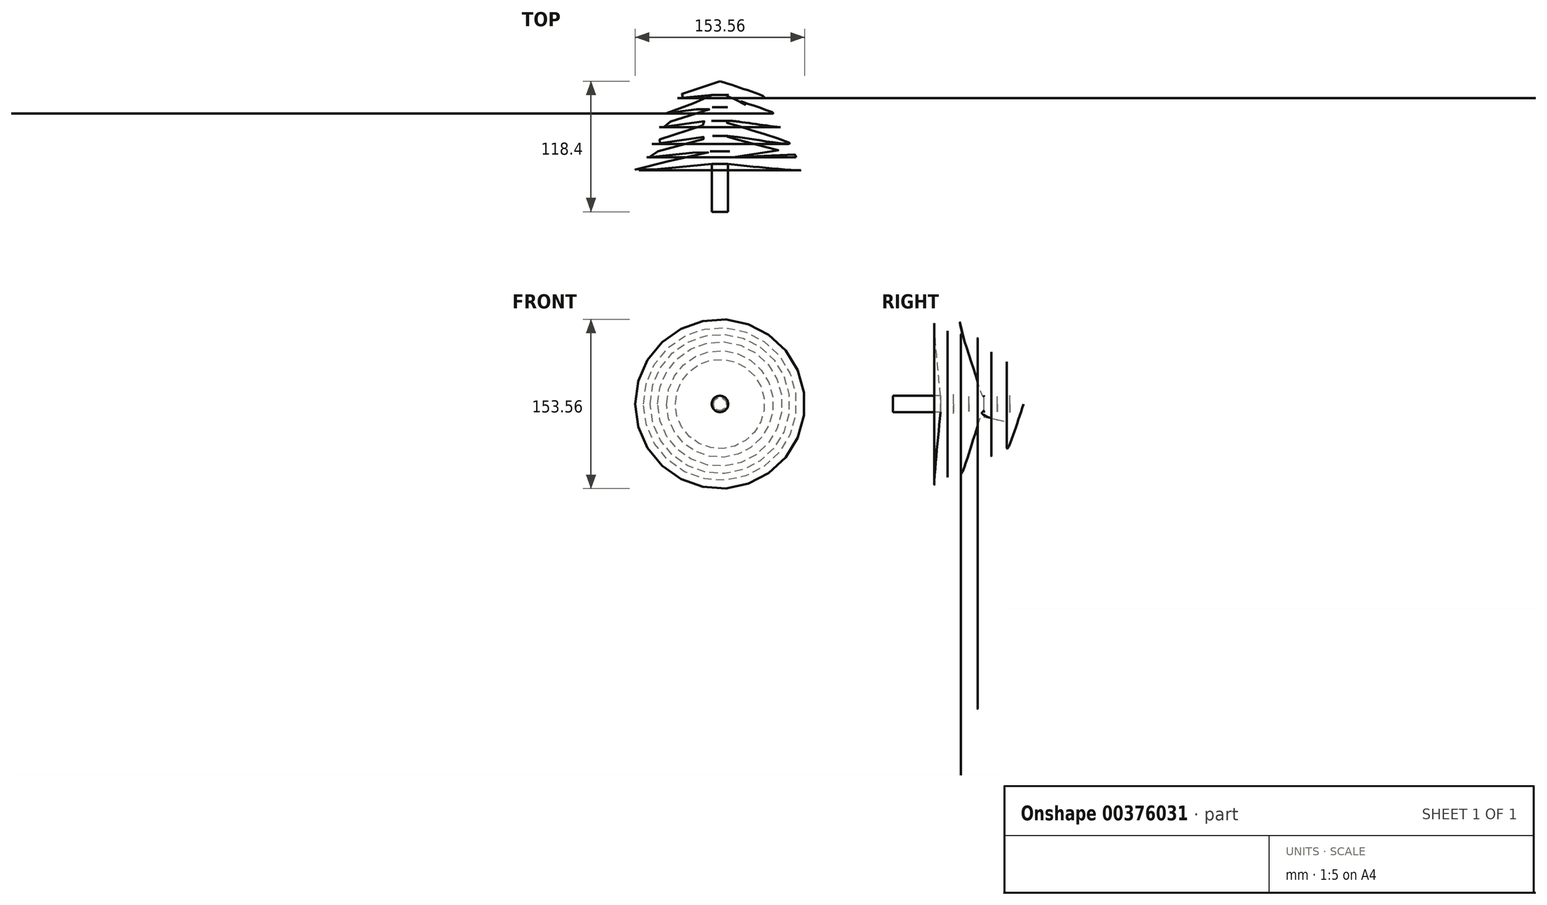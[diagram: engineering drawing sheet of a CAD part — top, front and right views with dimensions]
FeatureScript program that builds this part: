
annotation { "Feature Type Name" : "Feature", "Feature Type Description" : "" }
export const myFeature = defineFeature(function(context is Context, id is Id, definition is map)
    precondition{}
    {
        {
            var Q0;
            Q0=qCreatedBy(makeId("Top.planeOp"),FACE);
            var sketch = newSketch(context, id + "F0", { "sketchPlane" : qUnion([Q0])});
            skFitSpline(sketch, "E0", {"points": [v(0, 75.17) * mm, v(-39.36, 60) * mm, v(-5.8, 62.27) * mm, v(-48.4, 46.13) * mm, v(-6.13, 51.3) * mm, v(-56.46, 33.88) * mm, v(-6.13, 39.04) * mm, v(-63.23, 18.71) * mm, v(-6.13, 25.49) * mm, v(-69.36, 6.78) * mm, v(-8.07, 11.61) * mm, v(-75.17, -4.2) * mm, v(-7.42, 0) * mm], "startDerivative": vector(-927.97, -296.5) * mm, "endDerivative": vector(1244.58, 124.78) * mm});
            skLineSegment(sketch, "E1", {"start": v(-7.42, 0) * mm, "end": v(-7.42, -43.23) * mm});
            skLineSegment(sketch, "E2", {"start": v(-7.42, -43.23) * mm, "end": v(0, -43.23) * mm});
            skLineSegment(sketch, "E3", {"start": v(0, -43.23) * mm, "end": v(0, 75.17) * mm});
            skSolve(sketch);
        }
        {
            var Q0;
            Q0 = qSketchRegion(id + "F0", true);
            var Q1;
            Q1=sQuery(id+"F0.wireOp",EDGE,"E3");
            revolve(context, id + "F1", {"entities" : qUnion([Q0]), "axis" : qUnion([Q1]), "revolveType" : RevolveType.FULL});
        }
    });
